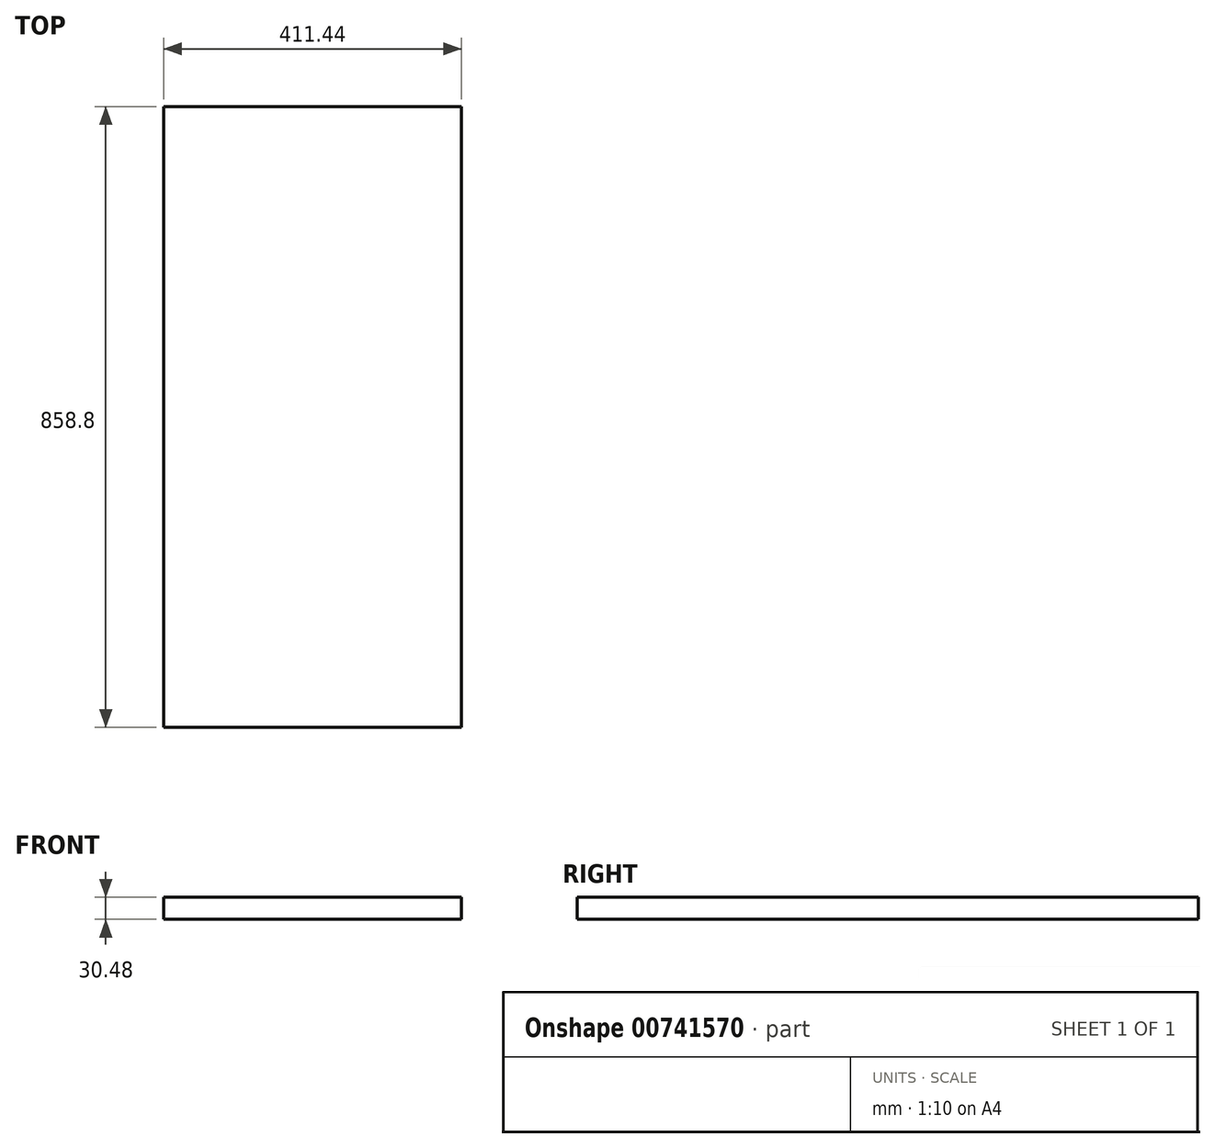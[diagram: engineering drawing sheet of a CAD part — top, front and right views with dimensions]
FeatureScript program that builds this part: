
annotation { "Feature Type Name" : "Feature", "Feature Type Description" : "" }
export const myFeature = defineFeature(function(context is Context, id is Id, definition is map)
    precondition{}
    {
        {
            var Q0;
            Q0=qCreatedBy(makeId("Top.planeOp"),FACE);
            var sketch = newSketch(context, id + "F0", { "sketchPlane" : qUnion([Q0])});
            skLineSegment(sketch, "E0.bottom", {"start": v(205.72, 429.4) * mm, "end": v(-205.72, 429.4) * mm});
            skLineSegment(sketch, "E0.top", {"start": v(205.72, -429.4) * mm, "end": v(-205.72, -429.4) * mm});
            skLineSegment(sketch, "E0.left", {"start": v(205.72, 429.4) * mm, "end": v(205.72, -429.4) * mm});
            skLineSegment(sketch, "E0.right", {"start": v(-205.72, 429.4) * mm, "end": v(-205.72, -429.4) * mm});
            skPoint(sketch, "E0.middle", {"position": v(0, 0) * mm});
            skSolve(sketch);
        }
        {
            var Q0;
            Q0 = qSketchRegion(id + "F0", true);
            extrude(context, id + "F1", {"entities" : qUnion([Q0]), "depth" : 30.48 * mm, "offsetDistance" : 25.4 * mm});
        }
    });
